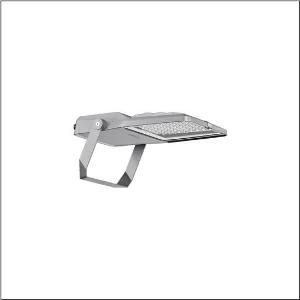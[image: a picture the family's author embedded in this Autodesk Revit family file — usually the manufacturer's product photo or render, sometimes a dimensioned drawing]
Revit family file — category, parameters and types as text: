
# Revit family: floodlight_fl_21_iq_mini___pl52_5xa7772d5d1a_a443
name_source: partatom
category: Lighting Fixtures
units: mm (PartAtom-declared; Revit-internal decimal feet)

## family parameters
Cut with Voids When Loaded = No
Host = Face
Light Source = No
Part Type = Normal
Room Calculation Point = No
Round Connector Dimension = Use Diameter
Shared = No

## types (1)
- --- (1 x LED, 16640 lm, 143 W, 4000K)
    Apparent Load = 143 VA
    CIE Flux Codes = 26 60 98 100 100
    Color Rendering = 80
    Color Temperature = 4000K
    Default Elevation = 1800 mm
    Description = Floodlight FL 21 iQ mini, floodlight, primary light control with lens, of PMMA, primary optical cover: protective disc, of toughened safety glass, transparent, light distribution: PL52, light emission: direct distribution, installation type: surface-mounted, LED, High Power LED, rated luminous flux: 16.640lm, luminous efficacy: 116lm/W, light colour: 840, colour temperature: 4000K, control: Street-Remote, Auto-Match, Temp-Guard, Night-Set, Smart-Wire, Desk-Remote (wireless, voltage-free reading and setting of iQ features in the workshop via application-optimized NFC function/RFID function), optimised constant luminous flux control (CLO 2.0), with terminal, 6-pole, mains connection: 220..240V, AC, 50/60Hz, start of lifetime: 143W, end of service life: 152W, reduction: 61W, luminaire housing, of diecast aluminium, powder-coated, Siteco® metallic grey (DB 702S), corrosivity category C5 mid according to DIN EN ISO 12944, sealing non-destructively replaceable, mounting bracket, of steel, galvanised, powder-coated, Siteco® metallic grey (DB 702S), protection rating (complete): IP66, insulation class (complete): insulation class II (safety insulation), certification: CE, ENEC, VDE, protection symbol: D, impact resistance: IK08, permissible operating ambient temperature: -40..+40°C, permissible operating ambient temperature for outdoor applications: -40..+50°C, standard: DIN EN 12944, LABS conformity tested according to VDMA 24364:2018-05, packaging unit: 1 piece

Light Distribution: PL52
    Height = 70 mm
    Lamp = 1 x LED
    Lamp Light Flux = 16640 lm
    Lamp Power = 143 W
    Lamp count = 1
    Length = 485 mm
    Luminous efficacy = 116 lm/W
    Manufacturer = Siteco
    ModVariant = No
    Model = 5XA7772D5D1A
    Number of Poles = 1
    OnlyDefault = Yes
    Power Factor = 1
    Product Name = Floodlight FL 21 iQ mini | PL52
    Product group = floodlight | pylon annexe
    ProductGroupID = 6200
    Protection Class = Protection class II
    Protection Degree = IP 66
    RLX_Detail_Level = 1
    RLX_Emergency_Light_Flux = 0 lm
    RLX_Emergency_Type = 0
    RLX_Emergency_Type_DB = No
    RlxData = <blob elided: 96677 chars, md5=0288bd1a>
    Socket = socket
    Standby Power = 0 W
    System Light Flux = 16640 lm
    System Power = 143 W
    Type Comments = factory setting: luminous flux: 100 % | dim-lin: 254 | 730 mA
    Type Image = l_1006845.jpg
    URL = http://relux.com
    VarID = @adj_095821
    Voltage = 0 V
    Weight = 0.00 kg
    Width = 337 mm

## geometry (parser evidence)
native form markers: Blend x4, Sweep x14
no freeform markers — native parametric forms only
